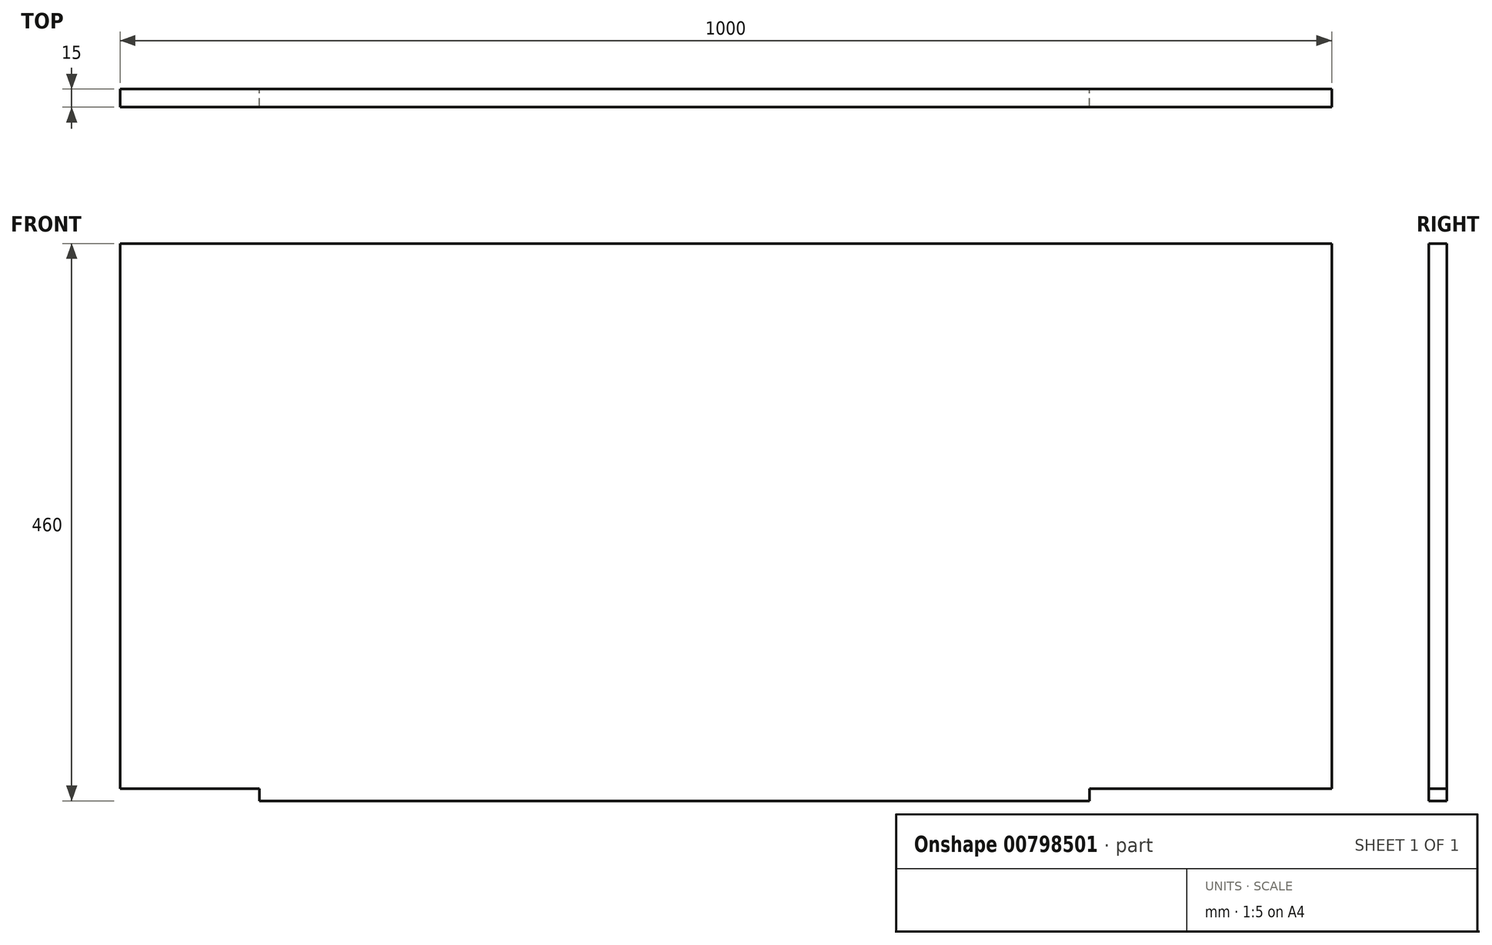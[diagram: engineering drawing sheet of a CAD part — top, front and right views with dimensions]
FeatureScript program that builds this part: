
annotation { "Feature Type Name" : "Feature", "Feature Type Description" : "" }
export const myFeature = defineFeature(function(context is Context, id is Id, definition is map)
    precondition{}
    {
        {
            var Q0;
            Q0=qCreatedBy(makeId("Front.planeOp"),FACE);
            var sketch = newSketch(context, id + "F0", { "sketchPlane" : qUnion([Q0])});
            skLineSegment(sketch, "E0.bottom", {"start": v(0, 0) * mm, "end": v(1000, 0) * mm});
            skLineSegment(sketch, "E0.top", {"start": v(0, -450) * mm, "end": v(1000, -450) * mm});
            skLineSegment(sketch, "E0.left", {"start": v(0, 0) * mm, "end": v(0, -450) * mm});
            skLineSegment(sketch, "E0.right", {"start": v(1000, 0) * mm, "end": v(1000, -450) * mm});
            skLineSegment(sketch, "E1.bottom", {"start": v(115, -450) * mm, "end": v(800, -450) * mm});
            skLineSegment(sketch, "E1.left", {"start": v(115, -450) * mm, "end": v(115, -460) * mm});
            skLineSegment(sketch, "E1.right", {"start": v(800, -450) * mm, "end": v(800, -460) * mm});
            skLineSegment(sketch, "E2", {"start": v(115, -460) * mm, "end": v(800, -460) * mm});
            skSolve(sketch);
        }
        {
            var Q0;
            {var subQ0=sQuery(id+"F0.wireOp",EDGE,"E1.left");Q0=qUnion([makeQuery(id+"F0.imprint","IMPRINT",FACE,{"disambiguationData":[TD([[makeQuery(id+"F0.imprint","IMPRINT",EDGE,{"derivedFrom":sQuery(id+"F0.wireOp",EDGE,"E0.bottom")}),-1.0]])]}),makeQuery(id+"F0.imprint","IMPRINT",FACE,{"disambiguationData":[TD([[makeQuery(id+"F0.imprint","IMPRINT",EDGE,{"derivedFrom":subQ0}),1.0]])]})]);}
            extrude(context, id + "F1", {"entities" : qUnion([Q0]), "depth" : 15 * mm, "offsetDistance" : 25 * mm});
        }
    });
